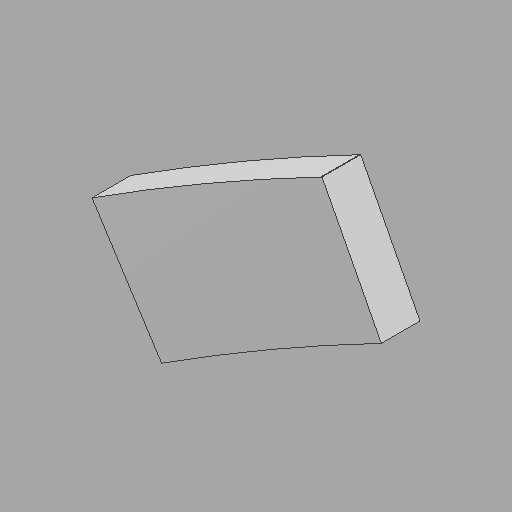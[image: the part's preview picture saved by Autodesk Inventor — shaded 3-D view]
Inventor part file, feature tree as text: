
AUTODESK INVENTOR PART (.ipt)
format: ipt  version: 2022.1 (Build 261234020, 234B)  size: 86,528 bytes
history: imported  units: in
note: dims shown in document units (in); Inventor stores cm internally (conversion verified against a paired STEP export)
features: imported_body x1
ambient origin geometry x8: Origin, YZ Plane, XZ Plane, XY Plane, X Axis, Y Axis, Z Axis, Center Point
bodies: Solid1 (imported_parasolid), Body1 (imported_parasolid)
feature tree (1):
  imported_body  NMx_Import_Brep_tag  [imported B-rep: ~7 faces, bbox_mm=[1140.79376, 952.251867, 152.4]]
